# Revit family: Door_Curtain_Wall-Outswing_With_Sidelite-Traco-NX-8910-One_Panel
name_source: partatom
category: Curtain Panels
revit_build: Autodesk Revit 2015 (Build: 20140905_0730(x64)
units: mm (PartAtom-declared; Revit-internal decimal feet)

## types (1)
- NX-8910 - One_Panel-Sidelite
    Allowable Air Infiltration Maximum = 0.1 @ 6.2 PSF
    Assembly Code = B2020220
    Condensation Resistance = 48
    Description = Single Door
    Designation = AAMA/WDMA/CSA 101/I.S.2/A-440-05: HS-C50 And AAMA/WDMA/CSA 101/I.S.2/A-440-08:AW-PG50-ATD
    Door Base = 0' - 1 1/8"
    Glazing Thickness = 0' - 0 3/8"
    Manufacturer = Traco
    Model = NX-8910
    Muntin Type = Muntin-Grid-Traco-Lites : Interior
    Product Documentation Link = http://www.alcoa.com
    Product Page URL = http://www.alcoa.com
    Product data url = https://bimobject.com
    Test Size = 48" X 96"
    Type Comments = 1 Panel With Sidelite
    U Factor = 0.40*
    URL = http://www.alcoa.com
    Uniform Load Deflection = 50.0000 psf
    Uniform Load Structural = 75.0000 psf
    Water Resistance = 15.0000 psf

## geometry (parser evidence)
native form markers: Blend x6, Sweep x20
no freeform markers — native parametric forms only
